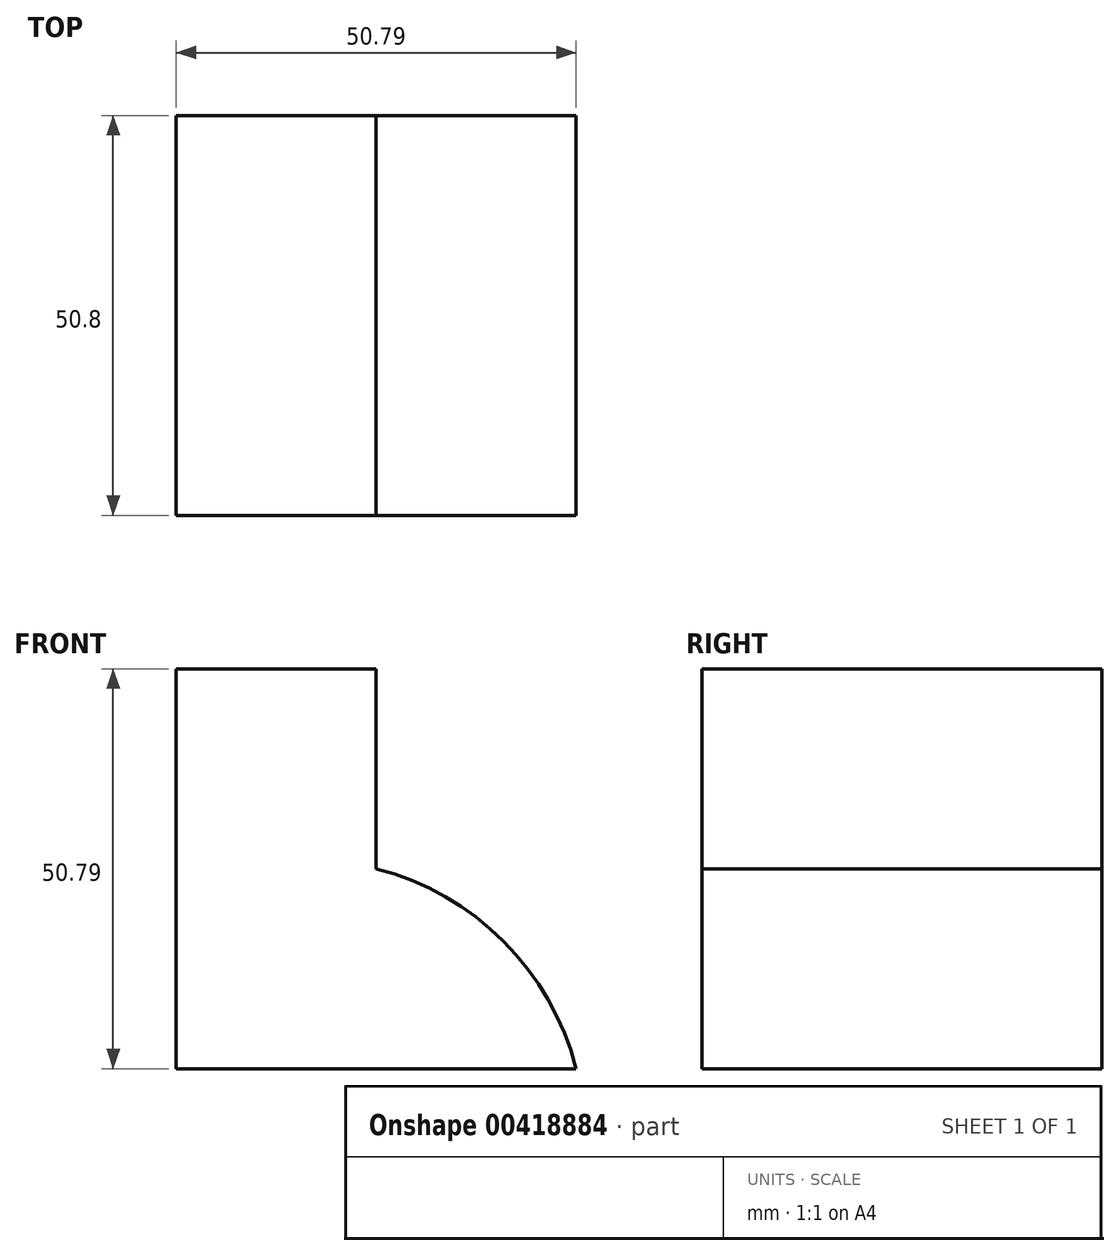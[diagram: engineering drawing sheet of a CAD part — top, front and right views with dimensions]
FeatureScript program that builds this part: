
annotation { "Feature Type Name" : "Feature", "Feature Type Description" : "" }
export const myFeature = defineFeature(function(context is Context, id is Id, definition is map)
    precondition{}
    {
        {
            var Q0;
            Q0=qCreatedBy(makeId("Front.planeOp"),FACE);
            var sketch = newSketch(context, id + "F0", { "sketchPlane" : qUnion([Q0])});
            skLineSegment(sketch, "E0", {"start": v(0, 0) * mm, "end": v(-50.8, 0) * mm});
            skLineSegment(sketch, "E1", {"start": v(-50.8, 0) * mm, "end": v(-50.8, 50.8) * mm});
            skLineSegment(sketch, "E2", {"start": v(-50.8, 50.8) * mm, "end": v(-25.4, 50.8) * mm});
            skLineSegment(sketch, "E3", {"start": v(-25.4, 50.8) * mm, "end": v(-25.4, 25.4) * mm});
            skArc(sketch, "E4", {"start": v(0, 0) * mm, "mid": v(-9.22, 16.18) * mm, "end": v(-25.4, 25.4) * mm});
            skSolve(sketch);
        }
        {
            var Q0;
            Q0 = qSketchRegion(id + "F0", true);
            extrude(context, id + "F1", {"entities" : qUnion([Q0]), "depth" : 50.8 * mm});
        }
    });
